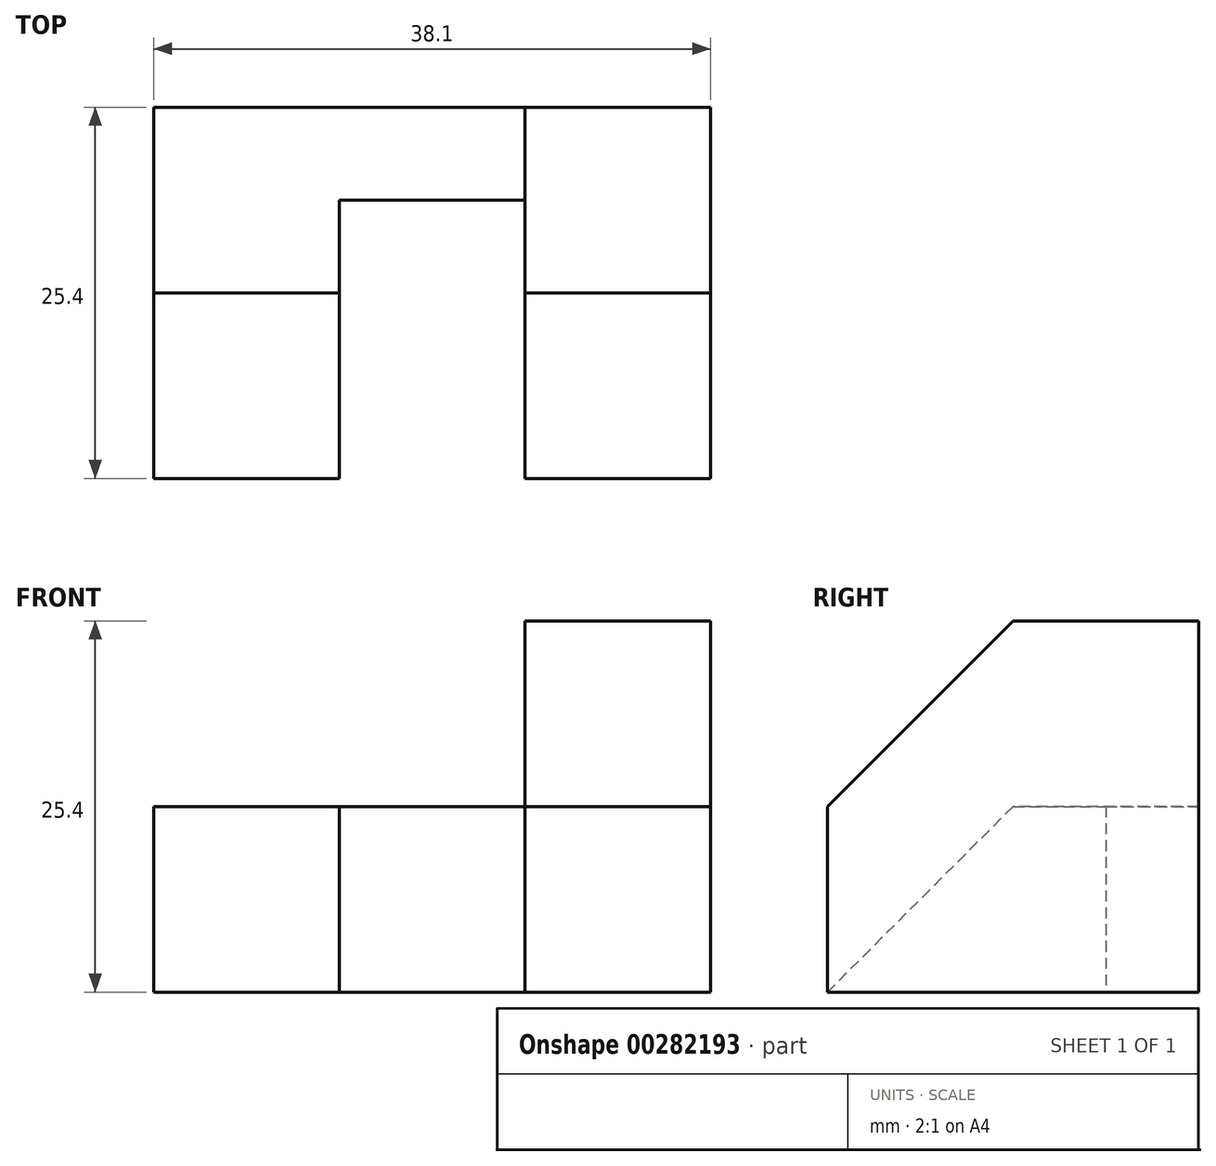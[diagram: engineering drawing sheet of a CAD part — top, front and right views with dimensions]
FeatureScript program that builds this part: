
annotation { "Feature Type Name" : "Feature", "Feature Type Description" : "" }
export const myFeature = defineFeature(function(context is Context, id is Id, definition is map)
    precondition{}
    {
        {
            var Q0;
            Q0=qCreatedBy(makeId("Right.planeOp"),FACE);
            var sketch = newSketch(context, id + "F0", { "sketchPlane" : qUnion([Q0])});
            skLineSegment(sketch, "E0.top", {"start": v(-12.7, 0) * mm, "end": v(12.7, 0) * mm});
            skLineSegment(sketch, "E0.left", {"start": v(-12.7, 12.7) * mm, "end": v(-12.7, 0) * mm});
            skLineSegment(sketch, "E1", {"start": v(12.7, 25.4) * mm, "end": v(0, 25.4) * mm});
            skLineSegment(sketch, "E2", {"start": v(0, 25.4) * mm, "end": v(-12.7, 12.7) * mm});
            skLineSegment(sketch, "E3", {"start": v(12.7, 0) * mm, "end": v(12.7, 25.4) * mm});
            skSolve(sketch);
        }
        {
            var Q0;
            Q0=makeQuery(id+"F0.imprint","IMPRINT",FACE,{"disambiguationData":[TD([[makeQuery(id+"F0.imprint","IMPRINT",EDGE,{"derivedFrom":sQuery(id+"F0.wireOp",EDGE,"E0.top")}),1.0]])]});
            extrude(context, id + "F1", {"entities" : qUnion([Q0]), "oppositeDirection" : true, "depth" : 12.7 * mm});
        }
        {
            var Q0;
            Q0=makeQuery(id+"F1.opExtrude","SWEPT_FACE",FACE,{"disambiguationData":[OSD([sQuery(id+"F0.wireOp",EDGE,"E0.top")])]});
            var sketch = newSketch(context, id + "F2", { "sketchPlane" : qUnion([Q0])});
            skLineSegment(sketch, "E4", {"start": v(-12.7, -12.7) * mm, "end": v(-38.1, -12.7) * mm});
            skLineSegment(sketch, "E5", {"start": v(-38.1, -12.7) * mm, "end": v(-38.1, 0) * mm});
            skLineSegment(sketch, "E6", {"start": v(-38.1, 0) * mm, "end": v(-25.4, 0) * mm});
            skLineSegment(sketch, "E7", {"start": v(-25.4, 0) * mm, "end": v(-25.4, -6.35) * mm});
            skLineSegment(sketch, "E8", {"start": v(-25.4, -6.35) * mm, "end": v(-12.7, -6.35) * mm});
            skSolve(sketch);
        }
        {
            var Q0;
            {var subQ0=sQuery(id+"F2.wireOp",EDGE,"E4");Q0=makeQuery(id+"F2.imprint","IMPRINT",FACE,{"disambiguationData":[TD([[makeQuery(id+"F2.imprint","IMPRINT",EDGE,{"derivedFrom":subQ0}),-1.0]])]});}
            extrude(context, id + "F3", {"entities" : qUnion([Q0]), "operationType" : NewBodyOperationType.ADD, "oppositeDirection" : true, "depth" : 12.7 * mm});
        }
        {
            var Q0;
            Q0=makeQuery(id+"F3.opExtrude","SWEPT_FACE",FACE,{"disambiguationData":[OSD([sQuery(id+"F2.wireOp",EDGE,"E5")])]});
            var sketch = newSketch(context, id + "F4", { "sketchPlane" : qUnion([Q0])});
            skLineSegment(sketch, "E9", {"start": v(0, 12.7) * mm, "end": v(12.7, 0) * mm});
            skLineSegment(sketch, "E10", {"start": v(12.7, 0) * mm, "end": v(0, 0) * mm});
            skLineSegment(sketch, "E11", {"start": v(0, 0) * mm, "end": v(0, 12.7) * mm});
            skSolve(sketch);
        }
        {
            var Q0;
            Q0=makeQuery(id+"F4.imprint","IMPRINT",FACE,{"disambiguationData":[TD([[makeQuery(id+"F4.imprint","IMPRINT",EDGE,{"derivedFrom":sQuery(id+"F4.wireOp",EDGE,"E9")}),-1.0]])]});
            extrude(context, id + "F5", {"entities" : qUnion([Q0]), "operationType" : NewBodyOperationType.ADD, "oppositeDirection" : true, "depth" : 12.7 * mm});
        }
    });
